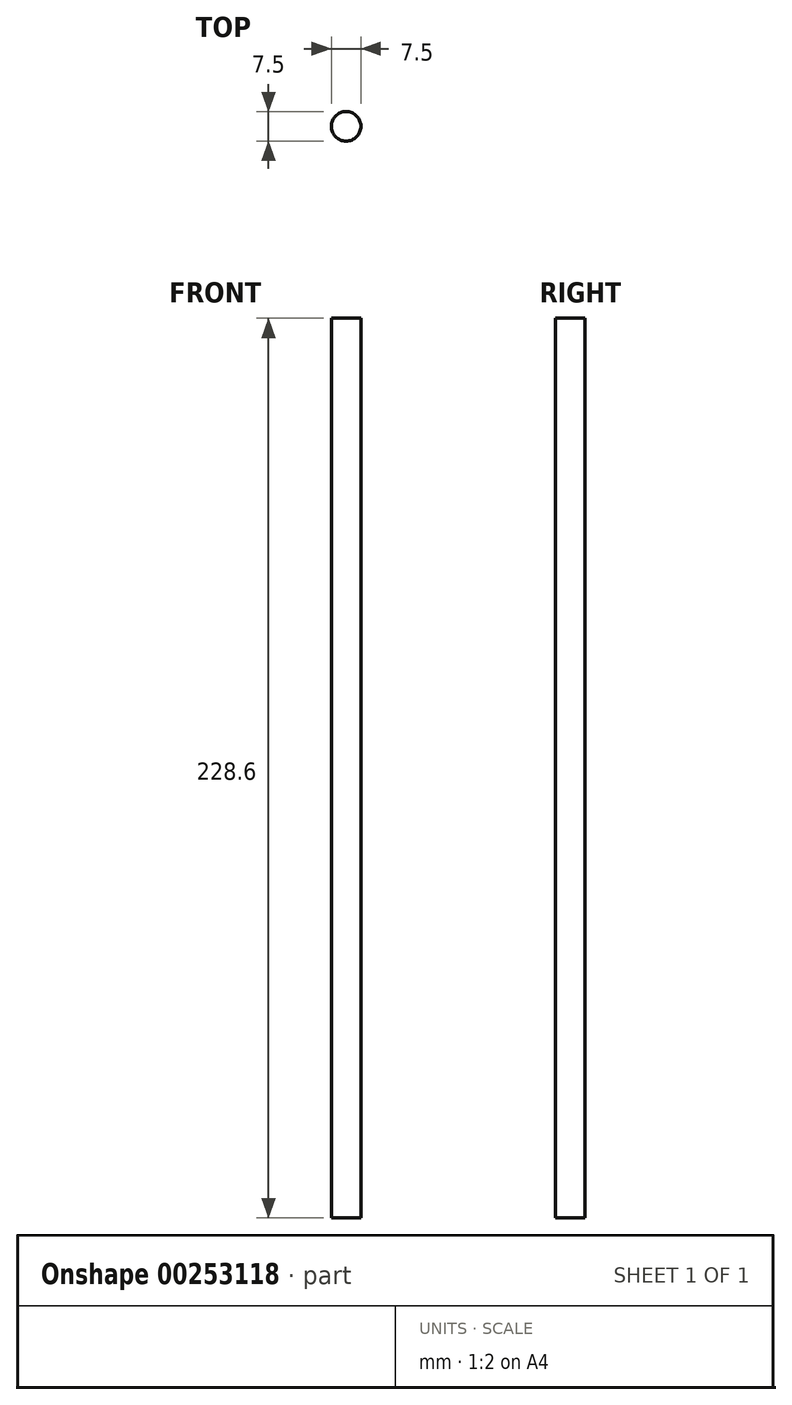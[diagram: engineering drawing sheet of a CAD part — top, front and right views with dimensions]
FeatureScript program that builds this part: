
annotation { "Feature Type Name" : "Feature", "Feature Type Description" : "" }
export const myFeature = defineFeature(function(context is Context, id is Id, definition is map)
    precondition{}
    {
        {
            var Q0;
            Q0=qCreatedBy(makeId("Top.planeOp"),FACE);
            var sketch = newSketch(context, id + "F0", { "sketchPlane" : qUnion([Q0])});
            skCircle(sketch, "E0", {"center": v(0, 0) * mm, "radius": 3.75 * mm});
            skSolve(sketch);
        }
        {
            var Q0;
            Q0 = qSketchRegion(id + "F0", true);
            extrude(context, id + "F1", {"entities" : qUnion([Q0]), "depth" : 228.6 * mm});
        }
    });
